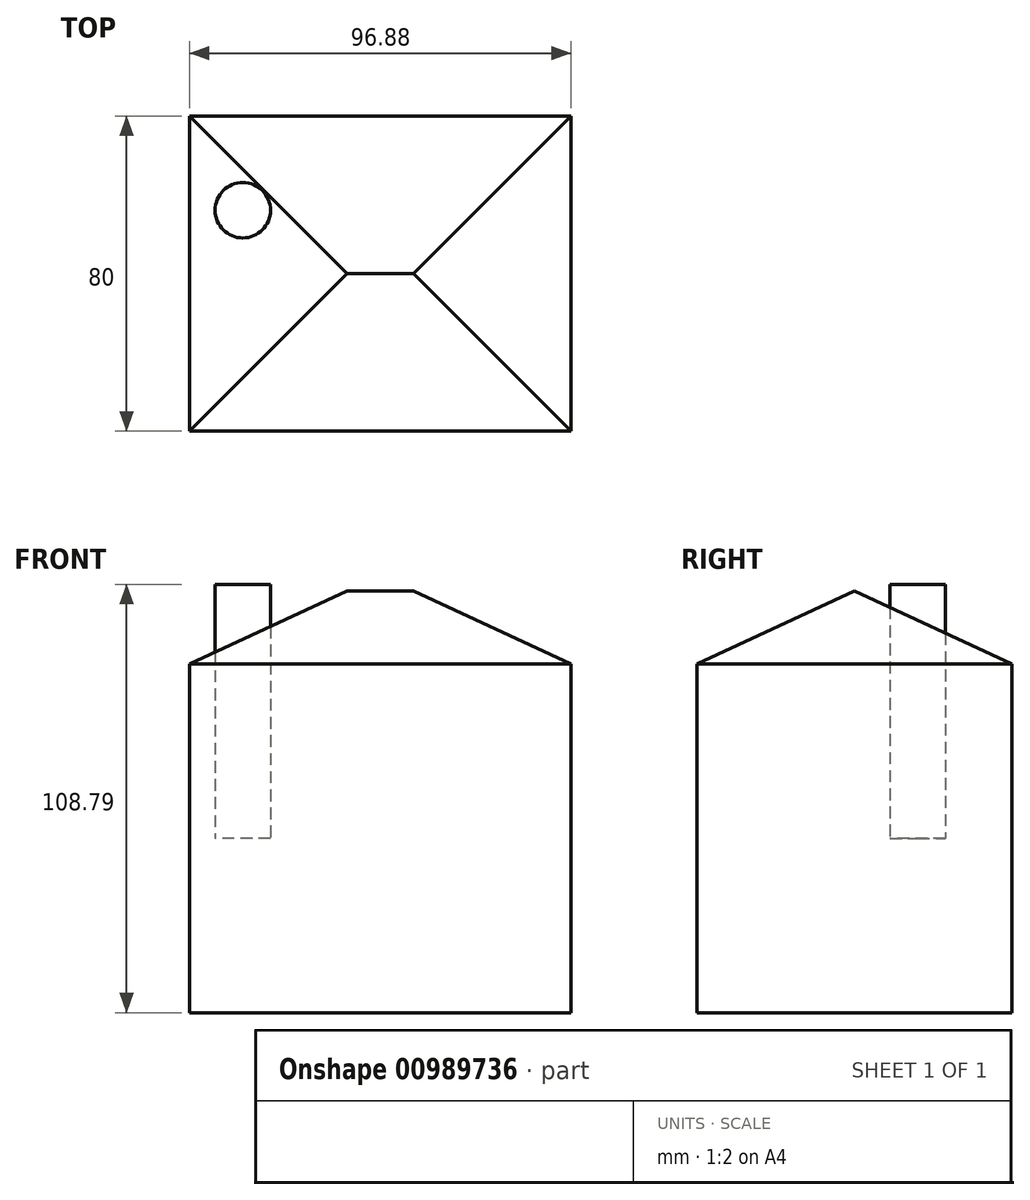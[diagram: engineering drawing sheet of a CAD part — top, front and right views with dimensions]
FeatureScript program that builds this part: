
annotation { "Feature Type Name" : "Feature", "Feature Type Description" : "" }
export const myFeature = defineFeature(function(context is Context, id is Id, definition is map)
    precondition{}
    {
        {
            var Q0;
            Q0=qCreatedBy(makeId("Front.planeOp"),FACE);
            var sketch = newSketch(context, id + "F0", { "sketchPlane" : qUnion([Q0])});
            skLineSegment(sketch, "E0.bottom", {"start": v(-48.44, 44.27) * mm, "end": v(48.44, 44.27) * mm});
            skLineSegment(sketch, "E0.top", {"start": v(-48.44, -44.27) * mm, "end": v(48.44, -44.27) * mm});
            skLineSegment(sketch, "E0.left", {"start": v(-48.44, 44.27) * mm, "end": v(-48.44, -44.27) * mm});
            skLineSegment(sketch, "E0.right", {"start": v(48.44, 44.27) * mm, "end": v(48.44, -44.27) * mm});
            skPoint(sketch, "E0.middle", {"position": v(0, 0) * mm});
            skSolve(sketch);
        }
        {
            var Q0;
            Q0=makeQuery(id+"F0.imprint","IMPRINT",FACE,{"disambiguationData":[TD([[makeQuery(id+"F0.imprint","IMPRINT",EDGE,{"derivedFrom":sQuery(id+"F0.wireOp",EDGE,"E0.bottom")}),-1.0]])]});
            extrude(context, id + "F1", {"entities" : qUnion([Q0]), "depth" : 40 * mm, "offsetDistance" : 25.4 * mm, "hasSecondDirection" : true, "secondDirectionOppositeDirection" : true, "secondDirectionDepth" : 40 * mm});
        }
        {
            var Q0;
            Q0=makeQuery(id+"F1.opExtrude","SWEPT_FACE",FACE,{"disambiguationData":[OSD([sQuery(id+"F0.wireOp",EDGE,"E0.bottom")])]});
            var sketch = newSketch(context, id + "F2", { "sketchPlane" : qUnion([Q0])});
            skLineSegment(sketch, "E1.0", {"start": v(48.44, 40) * mm, "end": v(-48.44, 40) * mm});
            skLineSegment(sketch, "E1.1", {"start": v(48.44, -40) * mm, "end": v(48.44, 40) * mm});
            skLineSegment(sketch, "E1.2", {"start": v(-48.44, -40) * mm, "end": v(48.44, -40) * mm});
            skLineSegment(sketch, "E1.3", {"start": v(-48.44, 40) * mm, "end": v(-48.44, -40) * mm});
            skSolve(sketch);
        }
        {
            var Q0;
            Q0=makeQuery(id+"F2.imprint","IMPRINT",FACE,{"disambiguationData":[TD([[makeQuery(id+"F2.imprint","IMPRINT",EDGE,{"derivedFrom":sQuery(id+"F2.wireOp",EDGE,"E1.0")}),-1.0]])]});
            extrude(context, id + "F3", {"entities" : qUnion([Q0]), "operationType" : NewBodyOperationType.ADD, "depth" : 25.4 * mm, "offsetDistance" : 25.4 * mm, "hasDraft" : true, "draftAngle" : 65 * degree, "draftPullDirection" : true});
        }
        {
            var Q0;
            Q0=qCreatedBy(makeId("Top.planeOp"),FACE);
            var sketch = newSketch(context, id + "F4", { "sketchPlane" : qUnion([Q0])});
            skCircle(sketch, "E2", {"center": v(-34.93, 16.09) * mm, "radius": 7.04 * mm});
            skSolve(sketch);
        }
        {
            var Q0;
            Q0 = qSketchRegion(id + "F4", true);
            var Q1;
            Q1=sQuery(id+"F4.wireOp",EDGE,"E2");
            extrude(context, id + "F5", {"entities" : qUnion([Q0]), "surfaceEntities" : qUnion([Q1]), "depth" : 64.52 * mm, "offsetDistance" : 25.4 * mm});
        }
    });
